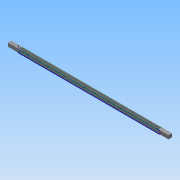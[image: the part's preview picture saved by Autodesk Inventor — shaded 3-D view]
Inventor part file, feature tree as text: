
AUTODESK INVENTOR PART (.ipt)
format: ipt  version: 2015 (Build 190159000, 159)  size: 2,233,344 bytes
history: native  units: in
note: dims shown in document units (in); Inventor stores cm internally (conversion verified against a paired STEP export)
features: sketch x5, other x4, projected_geometry x3, direct_edit x2, extrude x2, imported_body x1
ambient origin geometry x8: Origin, YZ Plane, XZ Plane, XY Plane, X Axis, Y Axis, Z Axis, Center Point
bodies: Body1 (feature_tree)
feature tree (17):
  parser-record x1  (decoder bookkeeping rows leaked as tree rows — omitted from the tree; the rows remain in map.json)
  other  "KKS10-10-51"
  sketch  "Sketch1"  dims[d2=0.0394in d6=-3.937in]
  direct_edit  "Direct Edit1"
  direct_edit  "Direct Edit2"
  sketch  "Sketch4"  dims[d7=-3.937in d10=0.0394in]
  sketch  "Sketch5"  dims[d11=0.3937in]
  extrude  "Extrusion1"  [1 undecoded]
  extrude  "Extrusion2"  Depth=0.0394in
  imported_body  "Base1"
  projected_geometry  "Projected Loop1"
  projected_geometry  "Projected Loop4"
  sketch  "Sketch6"  dims[d12=1.1811in]
  sketch  "Sketch7"  dims[d13=0.3937in d14=0.0in d15=0.9843in d16=0.3937in d17=0.3937in d18=0.0in]
  projected_geometry  "Projected Loop5"
  other  "Size1"
  other  "Size2"
note: 1 required parameter value undecoded (feature->parameter linkage not recoverable at this tier; creation-order binding heuristic only, values carry confidence <= 0.55)
